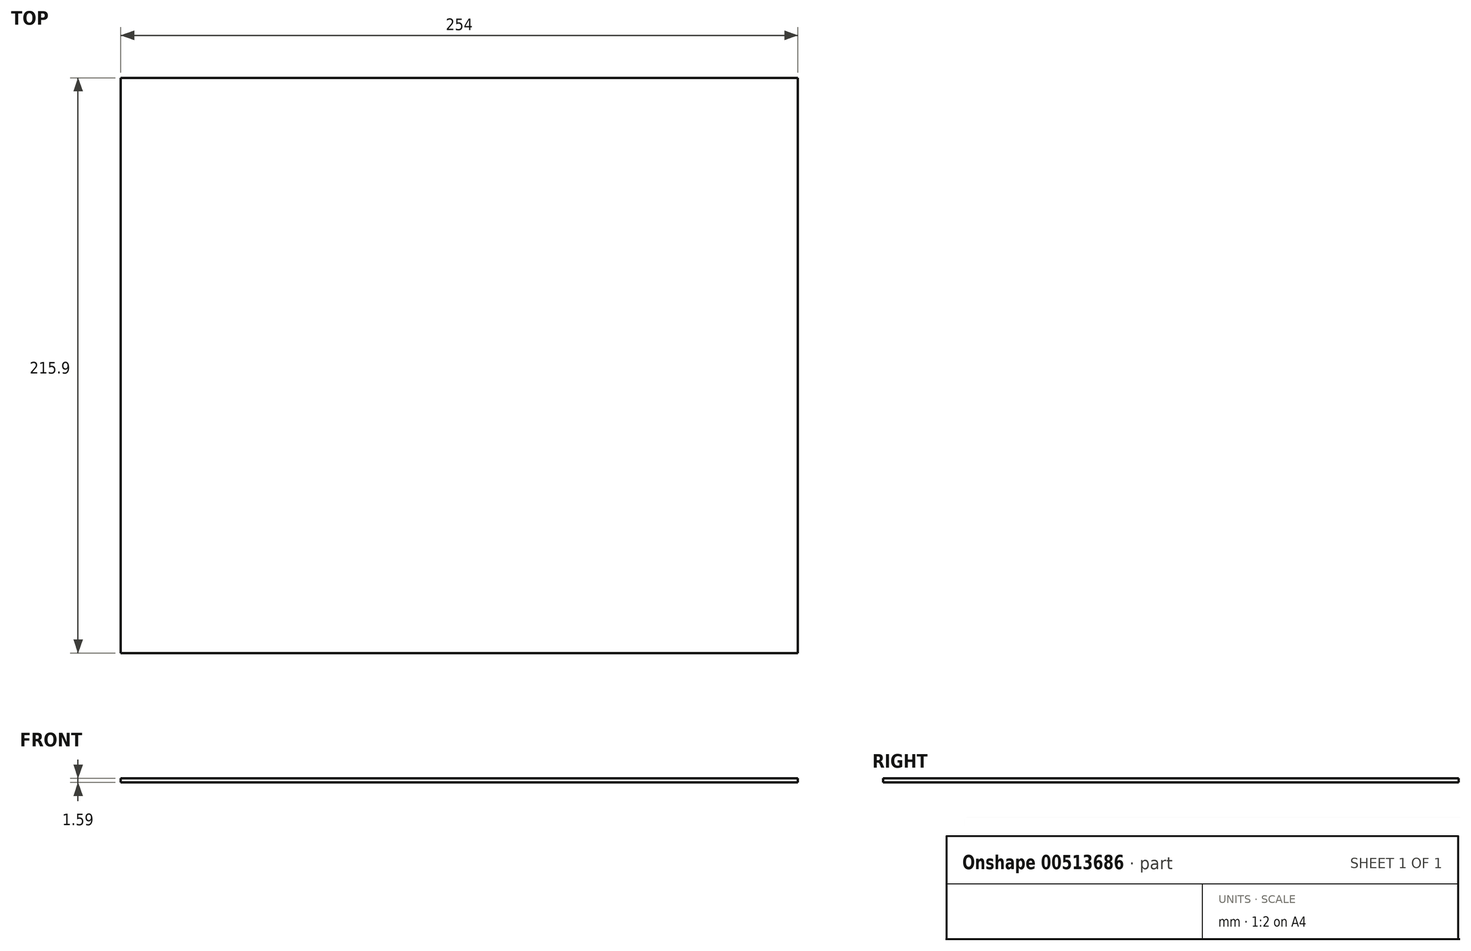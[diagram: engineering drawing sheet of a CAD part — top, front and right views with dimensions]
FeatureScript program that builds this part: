
annotation { "Feature Type Name" : "Feature", "Feature Type Description" : "" }
export const myFeature = defineFeature(function(context is Context, id is Id, definition is map)
    precondition{}
    {
        {
            var Q0;
            Q0=qCreatedBy(makeId("Top.planeOp"),FACE);
            var sketch = newSketch(context, id + "F0", { "sketchPlane" : qUnion([Q0])});
            skLineSegment(sketch, "E0.bottom", {"start": v(127, 107.95) * mm, "end": v(-127, 107.95) * mm});
            skLineSegment(sketch, "E0.top", {"start": v(127, -107.95) * mm, "end": v(-127, -107.95) * mm});
            skLineSegment(sketch, "E0.left", {"start": v(127, 107.95) * mm, "end": v(127, -107.95) * mm});
            skLineSegment(sketch, "E0.right", {"start": v(-127, 107.95) * mm, "end": v(-127, -107.95) * mm});
            skPoint(sketch, "E0.middle", {"position": v(0, 0) * mm});
            skSolve(sketch);
        }
        {
            var Q0;
            Q0=makeQuery(id+"F0.imprint","IMPRINT",FACE,{"disambiguationData":[TD([[makeQuery(id+"F0.imprint","IMPRINT",EDGE,{"derivedFrom":sQuery(id+"F0.wireOp",EDGE,"E0.bottom")}),1.0]])]});
            extrude(context, id + "F1", {"entities" : qUnion([Q0]), "depth" : 1.59 * mm});
        }
    });
